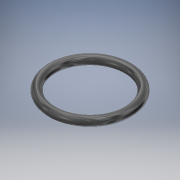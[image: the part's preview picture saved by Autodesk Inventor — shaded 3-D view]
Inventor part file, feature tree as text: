
AUTODESK INVENTOR PART (.ipt)
format: ipt  version: 2018 (Build 220112000, 112)  size: 164,352 bytes
history: native  units: mm (DEFAULTED — no unit token found)
features: revolve x1, sketch x1
ambient origin geometry x8: Origin, YZ Plane, XZ Plane, XY Plane, X Axis, Y Axis, Z Axis, Center Point
bodies: Solid1 (feature_tree)
feature tree (2):
  revolve  "Revolution1"  [1 undecoded]
  sketch  "Sketch2"  dims[d0=2.0mm d1=18.0mm d2=90.0deg]
note: 1 required parameter value undecoded (feature->parameter linkage not recoverable at this tier; creation-order binding heuristic only, values carry confidence <= 0.55)
